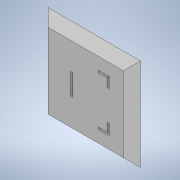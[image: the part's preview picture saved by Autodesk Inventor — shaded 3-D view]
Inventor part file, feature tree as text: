
AUTODESK INVENTOR PART (.ipt)
format: ipt  version: 2021 (Build 250183000, 183)  size: 146,432 bytes
history: native  units: in
note: dims shown in document units (in); Inventor stores cm internally (conversion verified against a paired STEP export)
features: chamfer x3, extrude x2, sketch x2
ambient origin geometry x8: Origin, YZ Plane, XZ Plane, XY Plane, X Axis, Y Axis, Z Axis, Center Point
bodies: Solid1 (feature_tree)
feature tree (7):
  extrude  "Extrusion1"  Depth=0.1575in
  chamfer  "Chamfer1"  Distance=0.1575in
  extrude  "Extrusion2"  Depth=0.1575in
  chamfer  "Chamfer2"  Distance=0.2756in
  chamfer  "Chamfer3"  Distance=1.3386in
  sketch  "Sketch1"  dims[d0=1.7008in d1=1.7008in d2=0.1575in d3=0.0in]
  sketch  "Sketch2"  dims[d4=0.1575in d5=0.0787in d6=45.0deg d7=0.0236in d8=0.2756in d9=1.3386in d10=0.315in d11=0.0394in d12=0.1969in d13=0.3937in d14=0.1969in d15=0.3937in d19=0.1969in d20=0.0394in d21=0.1575in d22=0.1575in d23=0.0394in d24=0.1969in d25=0.1969in d26=0.0197in d27=0.0in d28=0.0197in d29=0.0787in d30=45.0deg d31=0.0197in d32=0.0787in d33=45.0deg]
